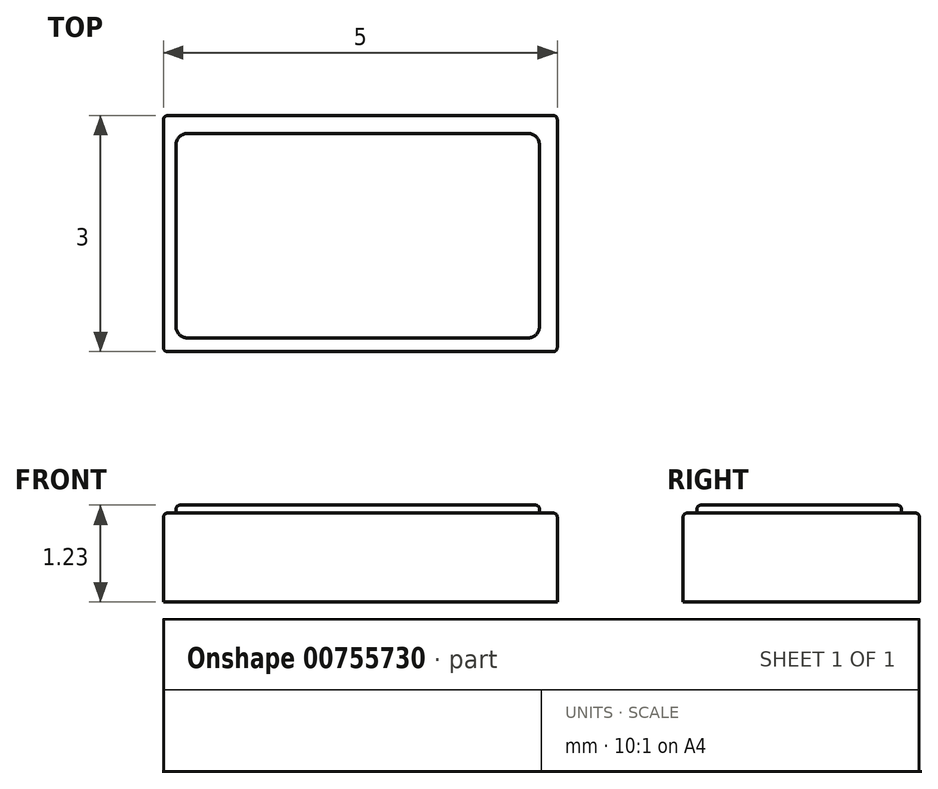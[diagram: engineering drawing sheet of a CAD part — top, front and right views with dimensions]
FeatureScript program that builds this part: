
annotation { "Feature Type Name" : "Feature", "Feature Type Description" : "" }
export const myFeature = defineFeature(function(context is Context, id is Id, definition is map)
    precondition{}
    {
        {
            var Q0;
            Q0=qCreatedBy(makeId("Top.planeOp"),FACE);
            var sketch = newSketch(context, id + "F0", { "sketchPlane" : qUnion([Q0])});
            skLineSegment(sketch, "E0.bottom", {"start": v(0, 0) * mm, "end": v(5, 0) * mm});
            skLineSegment(sketch, "E0.top", {"start": v(0, 3) * mm, "end": v(5, 3) * mm});
            skLineSegment(sketch, "E0.left", {"start": v(0, 0) * mm, "end": v(0, 3) * mm});
            skLineSegment(sketch, "E0.right", {"start": v(5, 0) * mm, "end": v(5, 3) * mm});
            skLineSegment(sketch, "E1", {"start": v(0, 1.5) * mm, "end": v(5, 1.5) * mm, "construction": true});
            skSolve(sketch);
        }
        {
            var Q0;
            Q0=makeQuery(id+"F0.imprint","IMPRINT",FACE,{"disambiguationData":[TD([[makeQuery(id+"F0.imprint","IMPRINT",EDGE,{"derivedFrom":sQuery(id+"F0.wireOp",EDGE,"E0.bottom")}),1.0]])]});
            extrude(context, id + "F1", {"entities" : qUnion([Q0]), "depth" : 1.13 * mm, "offsetDistance" : 25 * mm});
        }
        {
            var Q0;
            Q0=makeQuery(id+"F1.opExtrude","CAP_FACE",FACE,{"disambiguationData":[OSD([sQuery(id+"F0.wireOp",EDGE,"E0.bottom"),sQuery(id+"F0.wireOp",EDGE,"E0.top"),sQuery(id+"F0.wireOp",EDGE,"E0.left"),sQuery(id+"F0.wireOp",EDGE,"E0.right")])],"isStart":false});
            var sketch = newSketch(context, id + "F2", { "sketchPlane" : qUnion([Q0])});
            skLineSegment(sketch, "E2.bottom", {"start": v(0.3, 2.77) * mm, "end": v(4.63, 2.77) * mm});
            skLineSegment(sketch, "E2.top", {"start": v(0.3, 0.18) * mm, "end": v(4.63, 0.18) * mm});
            skLineSegment(sketch, "E2.left", {"start": v(0.16, 2.63) * mm, "end": v(0.16, 0.32) * mm});
            skLineSegment(sketch, "E2.right", {"start": v(4.77, 2.63) * mm, "end": v(4.77, 0.32) * mm});
            skPoint(sketch, "E3.visualSharp", {"position": v(0.16, 2.77) * mm});
            skArc(sketch, "E3.filletArc", {"start": v(0.3, 2.77) * mm, "mid": v(0.2, 2.73) * mm, "end": v(0.16, 2.63) * mm});
            skPoint(sketch, "E4.visualSharp", {"position": v(4.77, 2.77) * mm});
            skArc(sketch, "E4.filletArc", {"start": v(4.77, 2.63) * mm, "mid": v(4.73, 2.73) * mm, "end": v(4.63, 2.77) * mm});
            skPoint(sketch, "E5.visualSharp", {"position": v(4.77, 0.18) * mm});
            skArc(sketch, "E5.filletArc", {"start": v(4.63, 0.18) * mm, "mid": v(4.73, 0.22) * mm, "end": v(4.77, 0.32) * mm});
            skPoint(sketch, "E6.visualSharp", {"position": v(0.16, 0.18) * mm});
            skArc(sketch, "E6.filletArc", {"start": v(0.16, 0.32) * mm, "mid": v(0.2, 0.22) * mm, "end": v(0.3, 0.18) * mm});
            skSolve(sketch);
        }
        {
            var Q0;
            Q0=makeQuery(id+"F2.imprint","IMPRINT",FACE,{"disambiguationData":[TD([[makeQuery(id+"F2.imprint","IMPRINT",EDGE,{"derivedFrom":sQuery(id+"F2.wireOp",EDGE,"E2.bottom")}),-1.0]])]});
            extrude(context, id + "F3", {"entities" : qUnion([Q0]), "depth" : 0.1 * mm, "offsetDistance" : 25 * mm});
        }
        {
            var Q0;
            Q0=makeQuery(id+"F3.opExtrude","CAP_EDGE",EDGE,{"disambiguationData":[OSD([sQuery(id+"F2.wireOp",EDGE,"E2.bottom")])],"isStart":false});
            var Q1;
            Q1=makeQuery(id+"F3.opExtrude","CAP_EDGE",EDGE,{"disambiguationData":[OSD([sQuery(id+"F2.wireOp",EDGE,"E2.left")])],"isStart":false});
            var Q2;
            Q2=makeQuery(id+"F3.opExtrude","CAP_EDGE",EDGE,{"disambiguationData":[OSD([sQuery(id+"F2.wireOp",EDGE,"E2.top")])],"isStart":false});
            var Q3;
            Q3=makeQuery(id+"F3.opExtrude","CAP_EDGE",EDGE,{"disambiguationData":[OSD([sQuery(id+"F2.wireOp",EDGE,"E2.right")])],"isStart":false});
            var Q4;
            Q4=makeQuery(id+"F3.opExtrude","CAP_EDGE",EDGE,{"disambiguationData":[OSD([sQuery(id+"F2.wireOp",EDGE,"E4.filletArc")])],"isStart":false});
            var Q5;
            Q5=makeQuery(id+"F3.opExtrude","CAP_EDGE",EDGE,{"disambiguationData":[OSD([sQuery(id+"F2.wireOp",EDGE,"E5.filletArc")])],"isStart":false});
            var Q6;
            Q6=makeQuery(id+"F3.opExtrude","CAP_EDGE",EDGE,{"disambiguationData":[OSD([sQuery(id+"F2.wireOp",EDGE,"E6.filletArc")])],"isStart":false});
            var Q7;
            Q7=makeQuery(id+"F3.opExtrude","CAP_FACE",FACE,{"disambiguationData":[OSD([sQuery(id+"F2.wireOp",EDGE,"E2.bottom"),sQuery(id+"F2.wireOp",EDGE,"E2.top"),sQuery(id+"F2.wireOp",EDGE,"E2.left"),sQuery(id+"F2.wireOp",EDGE,"E2.right"),sQuery(id+"F2.wireOp",EDGE,"E3.filletArc"),sQuery(id+"F2.wireOp",EDGE,"E4.filletArc"),sQuery(id+"F2.wireOp",EDGE,"E5.filletArc"),sQuery(id+"F2.wireOp",EDGE,"E6.filletArc")])],"isStart":false});
            fillet(context, id + "F4", {"entities" : qUnion([Q0, Q1, Q2, Q3, Q4, Q5, Q6, Q7]), "radius" : 0.05 * mm, "tangentPropagation" : true, "allowEdgeOverflow" : false});
        }
        {
            var Q0;
            Q0=makeQuery(id+"F1.opExtrude","CAP_FACE",FACE,{"disambiguationData":[OSD([sQuery(id+"F0.wireOp",EDGE,"E0.bottom"),sQuery(id+"F0.wireOp",EDGE,"E0.top"),sQuery(id+"F0.wireOp",EDGE,"E0.left"),sQuery(id+"F0.wireOp",EDGE,"E0.right")])],"isStart":false});
            var Q1;
            Q1=makeQuery(id+"F1.opExtrude","SWEPT_EDGE",EDGE,{"disambiguationData":[OSD([sQuery(id+"F0.wireOp",EDGE,"E0.top"),sQuery(id+"F0.wireOp",EDGE,"E0.right")])]});
            var Q2;
            Q2=makeQuery(id+"F1.opExtrude","SWEPT_EDGE",EDGE,{"disambiguationData":[OSD([sQuery(id+"F0.wireOp",EDGE,"E0.bottom"),sQuery(id+"F0.wireOp",EDGE,"E0.right")])]});
            var Q3;
            Q3=makeQuery(id+"F1.opExtrude","SWEPT_EDGE",EDGE,{"disambiguationData":[OSD([sQuery(id+"F0.wireOp",EDGE,"E0.top"),sQuery(id+"F0.wireOp",EDGE,"E0.left")])]});
            var Q4;
            Q4=makeQuery(id+"F1.opExtrude","SWEPT_EDGE",EDGE,{"disambiguationData":[OSD([sQuery(id+"F0.wireOp",EDGE,"E0.bottom"),sQuery(id+"F0.wireOp",EDGE,"E0.left")])]});
            fillet(context, id + "F5", {"entities" : qUnion([Q0, Q1, Q2, Q3, Q4]), "radius" : 0.05 * mm, "tangentPropagation" : true, "allowEdgeOverflow" : false});
        }
    });
